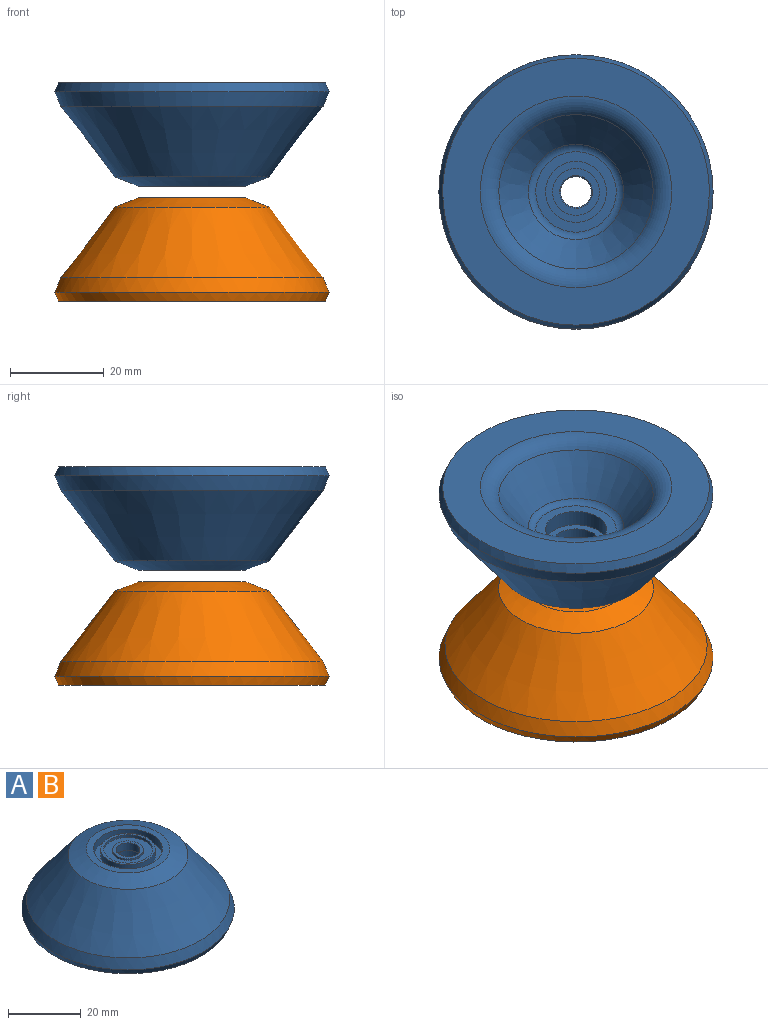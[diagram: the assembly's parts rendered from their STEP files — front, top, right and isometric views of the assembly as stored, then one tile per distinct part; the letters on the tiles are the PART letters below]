
ASSEMBLY  parts=2 mates=1
PART A: 24 faces, bbox 58.5x58.5x22 mm
  f0: cylinder r=3.3mm len=6.6mm, axis (0,0,1), area 51.8mm2, adj f19,f21
  f1: cylinder r=4.25mm len=8.5mm, axis (0,0,1), area 16mm2, adj f16,f19
  f2: plane 56.92x56.92mm, normal (0,0,-1), area 1231.4mm2, adj f14,f22
  f3: plane 23x23mm, normal (0,0,1), area 131.9mm2, adj f8,f23
  f4: cone r=28mm half-angle=37.4deg, axis (0,0,-1), area 2643.5mm2, adj f5,f23
  f5: cone r=30mm half-angle=21.8deg, axis (0,0,-1), area 608.9mm2, adj f4,f22
  f6: cone r=19.26mm half-angle=37.4deg, axis (0,0,-1), area 869.4mm2, adj f14,f20
  f7: plane 17.15x17.15mm, normal (0,0,-1), area 98.3mm2, adj f13,f20
  f8: cylinder r=9.5mm len=19mm, axis (0,0,1), area 149.2mm2, adj f3,f9
  f9: plane 19x19mm, normal (0,0,1), area 106.8mm2, adj f8,f10
  f10: cylinder r=7.5mm len=15mm, axis (0,0,1), area 117.8mm2, adj f9,f11
  f11: plane 15x15mm, normal (0,0,1), area 33.6mm2, adj f10,f15
  f12: plane 13x13mm, normal (0,0,-1), area 54.2mm2, adj f13,f18
  f13: cylinder r=6.5mm len=13mm, axis (0,0,-1), area 142.9mm2, adj f7,f12
  f14: torus R=20.45mm, axis (0,0,-1), area 528mm2, adj f2,f6
  f15: cylinder r=6.75mm len=13.5mm, axis (0,0,1), area 38.2mm2, adj f11,f16
  f16: plane 13.5x13.5mm, normal (0,0,1), area 86.4mm2, adj f1,f15
  f17: plane 10x10mm, normal (0,0,-1), area 40.1mm2, adj f18,f21
  f18: cylinder r=5mm len=10mm, axis (0,0,-1), area 141.4mm2, adj f12,f17
  f19: plane 8.5x8.5mm, normal (0,0,1), area 22.5mm2, adj f0,f1
  f20: torus R=8.58mm, axis (0,0,1), area 108.8mm2, adj f6,f7
  f21: cone r=3.5mm half-angle=45deg, axis (0,0,-1), area 6mm2, adj f0,f17
  f22: cone r=28.46mm half-angle=23.2deg, axis (0,0,1), area 366.3mm2, adj f2,f5
  f23: cone r=16.52mm half-angle=68.4deg, axis (0,0,-1), area 475.1mm2, adj f3,f4
PART B: same geometry as A
PLACE A rot(axis=(1,0,0),180deg) t=(35.49,29.38,26.87)mm
PLACE B t=(35.49,29.38,24.33)mm
MATE fastened A.f0 <-> B.f20  axis (0,0,-1) through (35.49,29.38,26.87)mm
